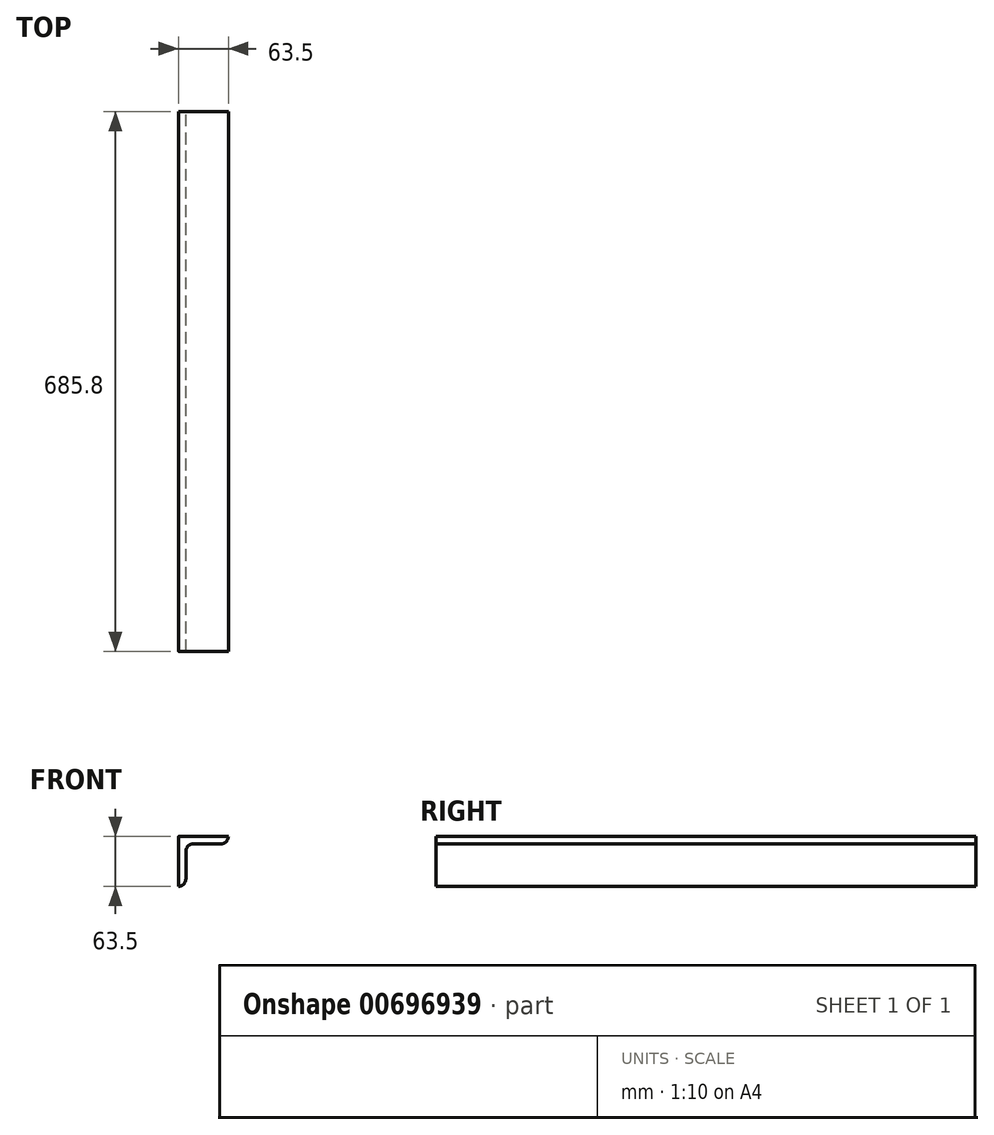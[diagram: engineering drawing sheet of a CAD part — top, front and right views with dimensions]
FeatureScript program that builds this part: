
annotation { "Feature Type Name" : "Feature", "Feature Type Description" : "" }
export const myFeature = defineFeature(function(context is Context, id is Id, definition is map)
    precondition{}
    {
        {
            var Q0;
            Q0=qCreatedBy(makeId("Front.planeOp"),FACE);
            var sketch = newSketch(context, id + "F0", { "sketchPlane" : qUnion([Q0])});
            skLineSegment(sketch, "E0", {"start": v(-26.79, 34.43) * mm, "end": v(-26.79, -28.81) * mm});
            skLineSegment(sketch, "E1", {"start": v(-26.79, -28.81) * mm, "end": v(-26.79, -28.81) * mm});
            skLineSegment(sketch, "E2", {"start": v(-17.26, -19.29) * mm, "end": v(-17.26, 15.64) * mm});
            skLineSegment(sketch, "E3", {"start": v(-7.74, 25.16) * mm, "end": v(27.19, 25.16) * mm});
            skLineSegment(sketch, "E4", {"start": v(-26.53, 34.69) * mm, "end": v(36.71, 34.69) * mm});
            skLineSegment(sketch, "E5", {"start": v(36.71, 34.69) * mm, "end": v(36.71, 34.69) * mm});
            skPoint(sketch, "E6.visualSharp", {"position": v(-17.26, 25.16) * mm});
            skArc(sketch, "E6.filletArc", {"start": v(-7.74, 25.16) * mm, "mid": v(-14.47, 22.37) * mm, "end": v(-17.26, 15.64) * mm});
            skPoint(sketch, "E7.visualSharp", {"position": v(-17.26, -28.81) * mm});
            skArc(sketch, "E7.filletArc", {"start": v(-26.79, -28.81) * mm, "mid": v(-20.05, -26.02) * mm, "end": v(-17.26, -19.29) * mm});
            skPoint(sketch, "E8.visualSharp", {"position": v(36.71, 25.16) * mm});
            skArc(sketch, "E8.filletArc", {"start": v(27.19, 25.16) * mm, "mid": v(33.92, 27.95) * mm, "end": v(36.71, 34.69) * mm});
            skPoint(sketch, "E9.visualSharp", {"position": v(-26.79, 34.69) * mm});
            skArc(sketch, "E9.filletArc", {"start": v(-26.53, 34.69) * mm, "mid": v(-26.71, 34.61) * mm, "end": v(-26.79, 34.43) * mm});
            skSolve(sketch);
        }
        {
            var Q0;
            Q0=makeQuery(id+"F0.imprint","IMPRINT",FACE,{"disambiguationData":[TD([[makeQuery(id+"F0.imprint","IMPRINT",EDGE,{"derivedFrom":sQuery(id+"F0.wireOp",EDGE,"E0")}),1.0]])]});
            extrude(context, id + "F1", {"entities" : qUnion([Q0]), "depth" : 685.8 * mm, "offsetDistance" : 25.4 * mm});
        }
    });
